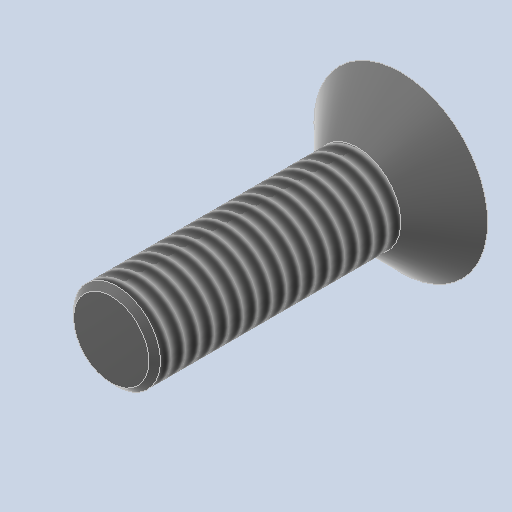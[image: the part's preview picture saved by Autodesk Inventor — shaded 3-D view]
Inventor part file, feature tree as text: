
AUTODESK INVENTOR PART (.ipt)
format: ipt  version: 2022 (Build 260153000, 153)  size: 175,104 bytes
history: native  units: in
note: dims shown in document units (in); Inventor stores cm internally (conversion verified against a paired STEP export)
features: sketch x2, revolve x1, chamfer x1, thread x1, extrude x1
ambient origin geometry x8: Origin, YZ Plane, XZ Plane, XY Plane, X Axis, Y Axis, Z Axis, Center Point
bodies: Body1 (feature_tree)
feature tree (6):
  revolve  "Revolution1"  [1 undecoded]
  chamfer  "Chamfer1"  Distance=0.1181in
  thread  "Thread1"  [1 undecoded]
  extrude  "Extrusion1"  Depth=0.0787in TaperAngle=45.0deg
  sketch  "Sketch1"  dims[d0=0.2362in d1=0.3937in]
  sketch  "Sketch2"  dims[d2=45.0deg d3=0.1181in d4=90.0deg d5=0.0079in d6=0.0787in d7=45.0deg d8=0.3268in d9=0.0in d10=0.0787in d11=0.0472in d12=0.0in]
note: 2 required parameter values undecoded (feature->parameter linkage not recoverable at this tier; creation-order binding heuristic only, values carry confidence <= 0.55)